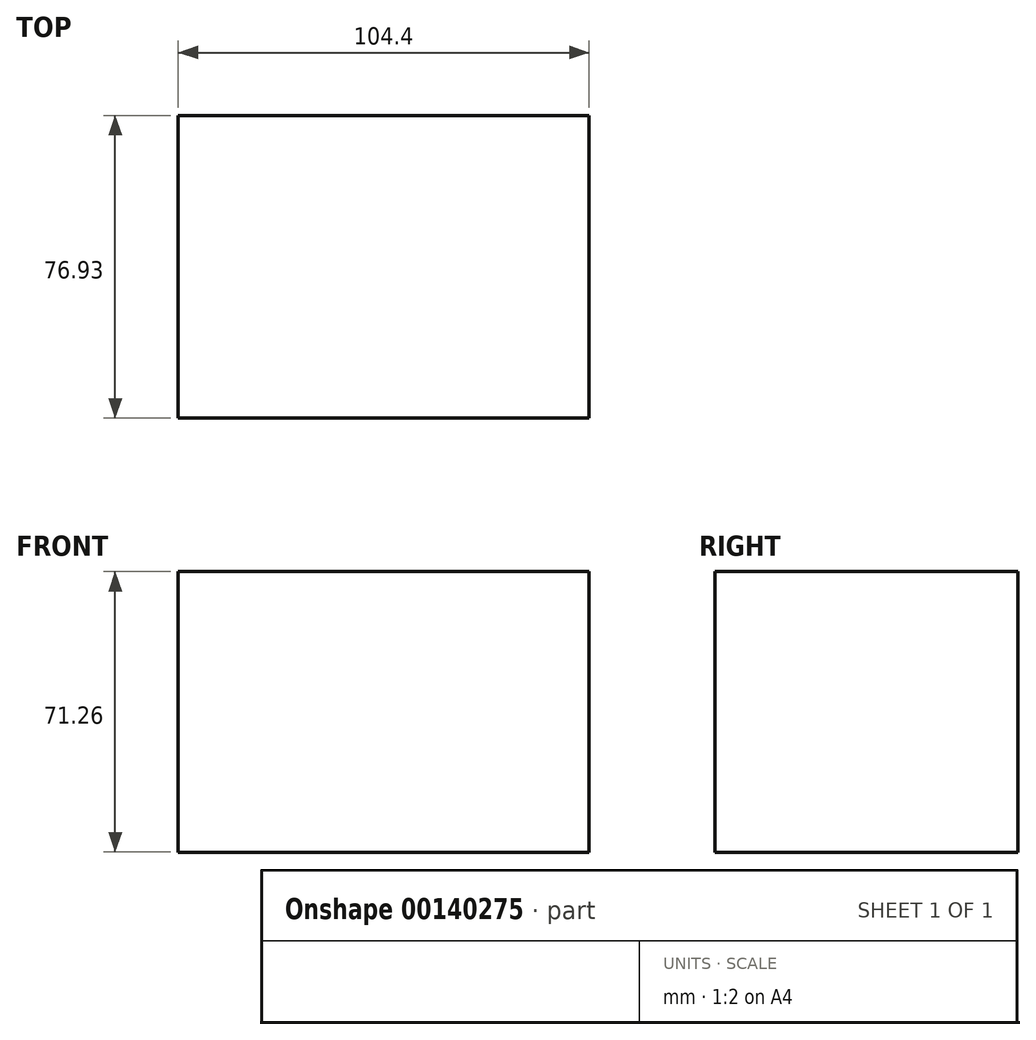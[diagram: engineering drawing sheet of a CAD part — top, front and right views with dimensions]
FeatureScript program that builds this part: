
annotation { "Feature Type Name" : "Feature", "Feature Type Description" : "" }
export const myFeature = defineFeature(function(context is Context, id is Id, definition is map)
    precondition{}
    {
        {
            var Q0;
            Q0=qCreatedBy(makeId("Front.planeOp"),FACE);
            var sketch = newSketch(context, id + "F0", { "sketchPlane" : qUnion([Q0])});
            skLineSegment(sketch, "E0.bottom", {"start": v(-55.7, 33.37) * mm, "end": v(48.7, 33.37) * mm});
            skLineSegment(sketch, "E0.top", {"start": v(-55.7, -37.9) * mm, "end": v(48.7, -37.9) * mm});
            skLineSegment(sketch, "E0.left", {"start": v(-55.7, 33.37) * mm, "end": v(-55.7, -37.9) * mm});
            skLineSegment(sketch, "E0.right", {"start": v(48.7, 33.37) * mm, "end": v(48.7, -37.9) * mm});
            skSolve(sketch);
        }
        {
            var Q0;
            Q0=makeQuery(id+"F0.imprint","IMPRINT",FACE,{"disambiguationData":[TD([[makeQuery(id+"F0.imprint","IMPRINT",EDGE,{"derivedFrom":sQuery(id+"F0.wireOp",EDGE,"E0.bottom")}),-1.0]])]});
            extrude(context, id + "F1", {"entities" : qUnion([Q0]), "depth" : 76.93 * mm});
        }
    });
